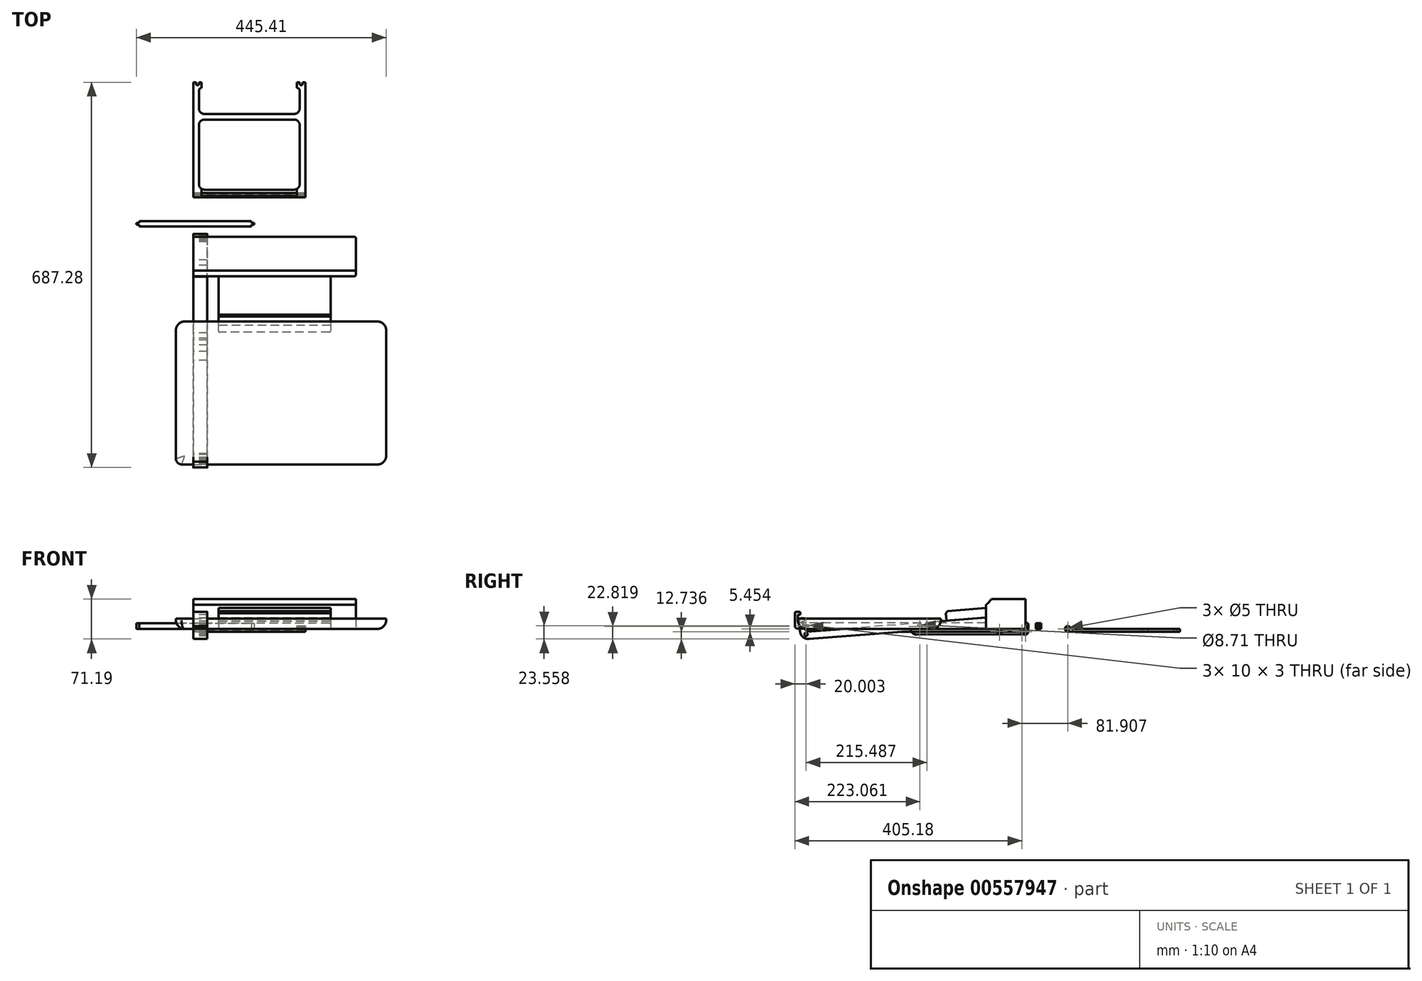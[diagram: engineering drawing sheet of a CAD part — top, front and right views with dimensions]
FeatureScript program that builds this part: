
annotation { "Feature Type Name" : "Feature", "Feature Type Description" : "" }
export const myFeature = defineFeature(function(context is Context, id is Id, definition is map)
    precondition{}
    {
        {
            var Q0;
            Q0=qCreatedBy(makeId("Top.planeOp"),FACE);
            var sketch = newSketch(context, id + "F0", { "sketchPlane" : qUnion([Q0])});
            skLineSegment(sketch, "E0", {"start": v(0, 0) * mm, "end": v(290, 0) * mm});
            skLineSegment(sketch, "E1", {"start": v(290, 0) * mm, "end": v(290, -70) * mm});
            skLineSegment(sketch, "E2", {"start": v(290, -70) * mm, "end": v(245, -70) * mm});
            skLineSegment(sketch, "E3", {"start": v(245, -70) * mm, "end": v(245, -170) * mm});
            skLineSegment(sketch, "E4", {"start": v(245, -170) * mm, "end": v(45, -170) * mm});
            skLineSegment(sketch, "E5", {"start": v(45, -170) * mm, "end": v(45, -70) * mm});
            skLineSegment(sketch, "E6", {"start": v(45, -70) * mm, "end": v(0, -70) * mm});
            skLineSegment(sketch, "E7", {"start": v(0, -70) * mm, "end": v(0, 0) * mm});
            skSolve(sketch);
        }
        {
            var Q0;
            Q0=makeQuery(id+"F0.imprint","IMPRINT",FACE,{"disambiguationData":[TD([[makeQuery(id+"F0.imprint","IMPRINT",EDGE,{"derivedFrom":sQuery(id+"F0.wireOp",EDGE,"E0")}),-1.0]])]});
            extrude(context, id + "F1", {"entities" : qUnion([Q0]), "depth" : 53 * mm, "offsetDistance" : 25.4 * mm});
        }
        {
            var Q0;
            Q0=makeQuery(id+"F1.opExtrude","SWEPT_FACE",FACE,{"disambiguationData":[OSD([sQuery(id+"F0.wireOp",EDGE,"E3")])]});
            var sketch = newSketch(context, id + "F2", { "sketchPlane" : qUnion([Q0])});
            skLineSegment(sketch, "E8", {"start": v(-170, 53) * mm, "end": v(-170, 10) * mm});
            skLineSegment(sketch, "E9", {"start": v(-170, 10) * mm, "end": v(-158, 13) * mm});
            skLineSegment(sketch, "E10", {"start": v(-158, 13) * mm, "end": v(-70, 20) * mm});
            skLineSegment(sketch, "E11", {"start": v(-70, 20) * mm, "end": v(-70, 43) * mm});
            skLineSegment(sketch, "E12", {"start": v(-70, 43) * mm, "end": v(-60, 53) * mm});
            skLineSegment(sketch, "E13", {"start": v(-60, 53) * mm, "end": v(-170, 53) * mm});
            skLineSegment(sketch, "E14", {"start": v(-70, 20) * mm, "end": v(-70.44, 37.02) * mm});
            skLineSegment(sketch, "E15", {"start": v(-70.44, 37.02) * mm, "end": v(-138.98, 31.57) * mm});
            skLineSegment(sketch, "E16", {"start": v(-138.98, 31.57) * mm, "end": v(-141.82, 27.51) * mm});
            skLineSegment(sketch, "E17", {"start": v(-141.82, 27.51) * mm, "end": v(-140.78, 14.37) * mm});
            skLineSegment(sketch, "E18", {"start": v(-140.78, 14.37) * mm, "end": v(-70, 20) * mm});
            skSolve(sketch);
        }
        {
            var Q0;
            Q0 = qSketchRegion(id + "F2", true);
            extrude(context, id + "F3", {"entities" : qUnion([Q0]), "depth" : 70 * mm, "offsetDistance" : 25 * mm, "hasSecondDirection" : true, "secondDirectionOppositeDirection" : true, "secondDirectionDepth" : 250 * mm});
        }
        {
            var Q0;
            Q0=makeQuery(id+"F3.opExtrude","SWEPT_BODY",BODY,{"disambiguationData":[OSD([sQuery(id+"F2.wireOp",EDGE,"E8"),sQuery(id+"F2.wireOp",EDGE,"E9"),sQuery(id+"F2.wireOp",EDGE,"E10"),sQuery(id+"F2.wireOp",EDGE,"E11"),sQuery(id+"F2.wireOp",EDGE,"E12"),sQuery(id+"F2.wireOp",EDGE,"E13")])]});
            var Q1;
            Q1=makeQuery(id+"F1.opExtrude","SWEPT_BODY",BODY,{"disambiguationData":[OSD([sQuery(id+"F0.wireOp",EDGE,"E0"),sQuery(id+"F0.wireOp",EDGE,"E1"),sQuery(id+"F0.wireOp",EDGE,"E2"),sQuery(id+"F0.wireOp",EDGE,"E3"),sQuery(id+"F0.wireOp",EDGE,"E4"),sQuery(id+"F0.wireOp",EDGE,"E5"),sQuery(id+"F0.wireOp",EDGE,"E6"),sQuery(id+"F0.wireOp",EDGE,"E7")])]});
            booleanBodies(context, id + "F4", {"operationType" : BooleanOperationType.SUBTRACTION, "tools" : qUnion([Q0]), "targets" : qUnion([Q1])});
        }
        {
            var Q0;
            Q0=makeQuery(id+"F1.opExtrude","SWEPT_EDGE",EDGE,{"disambiguationData":[OSD([sQuery(id+"F0.wireOp",EDGE,"E3"),sQuery(id+"F0.wireOp",EDGE,"E4")])]});
            var Q1;
            Q1=makeQuery(id+"F1.opExtrude","SWEPT_EDGE",EDGE,{"disambiguationData":[OSD([sQuery(id+"F0.wireOp",EDGE,"E1"),sQuery(id+"F0.wireOp",EDGE,"E2")])]});
            var Q2;
            Q2=makeQuery(id+"F1.opExtrude","SWEPT_EDGE",EDGE,{"disambiguationData":[OSD([sQuery(id+"F0.wireOp",EDGE,"E0"),sQuery(id+"F0.wireOp",EDGE,"E1")])]});
            var Q3;
            Q3=makeQuery(id+"F1.opExtrude","SWEPT_EDGE",EDGE,{"disambiguationData":[OSD([sQuery(id+"F0.wireOp",EDGE,"E0"),sQuery(id+"F0.wireOp",EDGE,"E7")])]});
            var Q4;
            Q4=makeQuery(id+"F1.opExtrude","SWEPT_EDGE",EDGE,{"disambiguationData":[OSD([sQuery(id+"F0.wireOp",EDGE,"E6"),sQuery(id+"F0.wireOp",EDGE,"E7")])]});
            var Q5;
            Q5=makeQuery(id+"F1.opExtrude","SWEPT_EDGE",EDGE,{"disambiguationData":[OSD([sQuery(id+"F0.wireOp",EDGE,"E4"),sQuery(id+"F0.wireOp",EDGE,"E5")])]});
            fillet(context, id + "F5", {"entities" : qUnion([Q0, Q1, Q2, Q3, Q4, Q5]), "radius" : 2 * mm, "tangentPropagation" : true, "allowEdgeOverflow" : false});
        }
        {
            var Q0;
            Q0=qCreatedBy(makeId("Right.planeOp"),FACE);
            var sketch = newSketch(context, id + "F6", { "sketchPlane" : qUnion([Q0])});
            skLineSegment(sketch, "E19", {"start": v(0.07, 10.37) * mm, "end": v(0.07, 0.37) * mm});
            skLineSegment(sketch, "E20", {"start": v(0.07, 0.37) * mm, "end": v(-70.93, 0.37) * mm});
            skLineSegment(sketch, "E21", {"start": v(-70.93, 0.37) * mm, "end": v(-70.93, 10.37) * mm});
            skLineSegment(sketch, "E22", {"start": v(-70.93, 10.37) * mm, "end": v(-396.42, 10.37) * mm});
            skLineSegment(sketch, "E23", {"start": v(-406.42, 20.37) * mm, "end": v(-406.42, 25.18) * mm});
            skLineSegment(sketch, "E24", {"start": v(-403.42, 30.18) * mm, "end": v(-409.42, 30.18) * mm});
            skLineSegment(sketch, "E25", {"start": v(-411.42, 28.18) * mm, "end": v(-411.42, 4.95) * mm});
            skLineSegment(sketch, "E26", {"start": v(-406.43, 0.37) * mm, "end": v(-206.4, 0.37) * mm});
            skLineSegment(sketch, "E27", {"start": v(5.07, 0.23) * mm, "end": v(5.07, 8.37) * mm});
            skLineSegment(sketch, "E28", {"start": v(3.07, 10.37) * mm, "end": v(0.07, 10.37) * mm});
            skPoint(sketch, "E29.visualSharp", {"position": v(-406.42, 10.37) * mm});
            skArc(sketch, "E29.filletArc", {"start": v(-406.42, 20.37) * mm, "mid": v(-403.49, 13.3) * mm, "end": v(-396.42, 10.37) * mm});
            skPoint(sketch, "E30.visualSharp", {"position": v(5.07, -9.63) * mm});
            skArc(sketch, "E30.filletArc", {"start": v(-6.24, -9.69) * mm, "mid": v(1.66, -7.3) * mm, "end": v(5.07, 0.23) * mm});
            skPoint(sketch, "E31.visualSharp", {"position": v(-411.42, 30.18) * mm});
            skArc(sketch, "E31.filletArc", {"start": v(-409.42, 30.18) * mm, "mid": v(-410.83, 29.6) * mm, "end": v(-411.42, 28.18) * mm});
            skPoint(sketch, "E32.visualSharp", {"position": v(5.07, 10.37) * mm});
            skArc(sketch, "E32.filletArc", {"start": v(5.07, 8.37) * mm, "mid": v(4.48, 9.78) * mm, "end": v(3.07, 10.37) * mm});
            skLineSegment(sketch, "E33.bottom", {"start": v(-386.42, 6.87) * mm, "end": v(-396.42, 6.87) * mm});
            skLineSegment(sketch, "E33.top", {"start": v(-386.42, 3.87) * mm, "end": v(-396.42, 3.87) * mm});
            skLineSegment(sketch, "E33.left", {"start": v(-386.42, 6.87) * mm, "end": v(-386.42, 3.87) * mm});
            skLineSegment(sketch, "E33.right", {"start": v(-396.42, 6.87) * mm, "end": v(-396.42, 3.87) * mm});
            skLineSegment(sketch, "E34.filletArc", {"start": v(-380.93, 2.65) * mm, "end": v(-380.93, 2.65) * mm});
            skLineSegment(sketch, "E35.bottom", {"start": v(-170.93, 6.87) * mm, "end": v(-180.93, 6.87) * mm});
            skLineSegment(sketch, "E35.top", {"start": v(-170.93, 3.87) * mm, "end": v(-180.93, 3.87) * mm});
            skLineSegment(sketch, "E35.left", {"start": v(-170.93, 6.87) * mm, "end": v(-170.93, 3.87) * mm});
            skLineSegment(sketch, "E35.right", {"start": v(-180.93, 6.87) * mm, "end": v(-180.93, 3.87) * mm});
            skLineSegment(sketch, "E36.bottom", {"start": v(-40.88, -3.13) * mm, "end": v(-50.88, -3.13) * mm});
            skLineSegment(sketch, "E36.top", {"start": v(-40.88, -6.13) * mm, "end": v(-50.88, -6.13) * mm});
            skLineSegment(sketch, "E36.left", {"start": v(-40.88, -3.13) * mm, "end": v(-40.88, -6.13) * mm});
            skLineSegment(sketch, "E36.right", {"start": v(-50.88, -3.13) * mm, "end": v(-50.88, -6.13) * mm});
            skCircle(sketch, "E37", {"center": v(-6.24, -4.69) * mm, "radius": 2.5 * mm});
            skLineSegment(sketch, "E38", {"start": v(-194.37, -10.19) * mm, "end": v(-6.24, -9.69) * mm});
            skLineSegment(sketch, "E39", {"start": v(-406.42, 25.18) * mm, "end": v(-403.42, 25.18) * mm});
            skLineSegment(sketch, "E40", {"start": v(-401.42, 27.18) * mm, "end": v(-401.42, 28.18) * mm});
            skPoint(sketch, "E41.visualSharp", {"position": v(-401.42, 30.18) * mm});
            skArc(sketch, "E41.filletArc", {"start": v(-401.42, 28.18) * mm, "mid": v(-402, 29.6) * mm, "end": v(-403.42, 30.18) * mm});
            skPoint(sketch, "E42.visualSharp", {"position": v(-401.42, 25.18) * mm});
            skArc(sketch, "E42.filletArc", {"start": v(-403.42, 25.18) * mm, "mid": v(-402, 25.77) * mm, "end": v(-401.42, 27.18) * mm});
            skLineSegment(sketch, "E43", {"start": v(-204.4, -0.19) * mm, "end": v(-204.4, -1.63) * mm});
            skPoint(sketch, "E44.visualSharp", {"position": v(-204.4, -10.21) * mm});
            skArc(sketch, "E44.filletArc", {"start": v(-204.4, -0.19) * mm, "mid": v(-201.46, -7.27) * mm, "end": v(-194.37, -10.19) * mm});
            skPoint(sketch, "E45.visualSharp", {"position": v(-204.4, 0.37) * mm});
            skArc(sketch, "E45.filletArc", {"start": v(-204.4, -1.63) * mm, "mid": v(-204.98, -0.22) * mm, "end": v(-206.4, 0.37) * mm});
            skArc(sketch, "E46", {"start": v(-411.42, 4.95) * mm, "mid": v(-409.82, 1.69) * mm, "end": v(-406.43, 0.37) * mm});
            skSolve(sketch);
        }
        {
            var Q0;
            Q0=makeQuery(id+"F6.imprint","IMPRINT",FACE,{"disambiguationData":[TD([[makeQuery(id+"F6.imprint","IMPRINT",EDGE,{"derivedFrom":sQuery(id+"F6.wireOp",EDGE,"E19")}),1.0]])]});
            extrude(context, id + "F7", {"entities" : qUnion([Q0]), "depth" : 25 * mm, "offsetDistance" : 25 * mm});
        }
        {
            var Q0;
            Q0=qCreatedBy(makeId("Top.planeOp"),FACE);
            var sketch = newSketch(context, id + "F8", { "sketchPlane" : qUnion([Q0])});
            skLineSegment(sketch, "E47", {"start": v(103.7, 27.93) * mm, "end": v(-96.3, 27.93) * mm});
            skLineSegment(sketch, "E48", {"start": v(-96.3, 27.93) * mm, "end": v(-96.3, 24.93) * mm});
            skLineSegment(sketch, "E49", {"start": v(-96.3, 24.93) * mm, "end": v(-101.3, 24.93) * mm});
            skLineSegment(sketch, "E50", {"start": v(-101.3, 24.93) * mm, "end": v(-101.3, 21.93) * mm});
            skLineSegment(sketch, "E51", {"start": v(-101.3, 21.93) * mm, "end": v(-96.3, 21.93) * mm});
            skLineSegment(sketch, "E52", {"start": v(-96.3, 21.93) * mm, "end": v(-96.3, 18.93) * mm});
            skLineSegment(sketch, "E53", {"start": v(-96.3, 18.93) * mm, "end": v(103.7, 18.93) * mm});
            skLineSegment(sketch, "E54", {"start": v(103.7, 18.93) * mm, "end": v(103.7, 21.93) * mm});
            skLineSegment(sketch, "E55", {"start": v(103.7, 21.93) * mm, "end": v(108.7, 21.93) * mm});
            skLineSegment(sketch, "E56", {"start": v(108.7, 21.93) * mm, "end": v(108.7, 24.93) * mm});
            skLineSegment(sketch, "E57", {"start": v(108.7, 24.93) * mm, "end": v(103.7, 24.93) * mm});
            skLineSegment(sketch, "E58", {"start": v(103.7, 24.93) * mm, "end": v(103.7, 27.93) * mm});
            skSolve(sketch);
        }
        {
            var Q0;
            Q0 = qSketchRegion(id + "F8", true);
            extrude(context, id + "F9", {"entities" : qUnion([Q0]), "depth" : 10 * mm, "offsetDistance" : 25 * mm});
        }
        {
            var Q0;
            Q0=qCreatedBy(makeId("Right.planeOp"),FACE);
            var sketch = newSketch(context, id + "F10", { "sketchPlane" : qUnion([Q0])});
            skLineSegment(sketch, "E59.bottom", {"start": v(71.73, 71.48) * mm, "end": v(83.68, 71.48) * mm});
            skLineSegment(sketch, "E59.top", {"start": v(71.73, 63) * mm, "end": v(83.68, 63) * mm});
            skLineSegment(sketch, "E59.left", {"start": v(71.73, 71.48) * mm, "end": v(71.73, 63) * mm});
            skLineSegment(sketch, "E59.right", {"start": v(83.68, 71.48) * mm, "end": v(83.68, 63) * mm});
            skLineSegment(sketch, "E60", {"start": v(-71, 19.86) * mm, "end": v(-382.03, -4.78) * mm});
            skLineSegment(sketch, "E61", {"start": v(-398.16, 8.99) * mm, "end": v(-398.56, 13.97) * mm});
            skLineSegment(sketch, "E62", {"start": v(-398.56, 13.97) * mm, "end": v(-395.57, 14.2) * mm});
            skLineSegment(sketch, "E63", {"start": v(-393.73, 16.36) * mm, "end": v(-393.81, 17.36) * mm});
            skLineSegment(sketch, "E64", {"start": v(-395.96, 19.2) * mm, "end": v(-398.95, 18.95) * mm});
            skLineSegment(sketch, "E65", {"start": v(-403.54, 13.57) * mm, "end": v(-402.12, -4.38) * mm});
            skLineSegment(sketch, "E66", {"start": v(-385.98, -18.14) * mm, "end": v(-220.07, -5) * mm});
            skLineSegment(sketch, "E67", {"start": v(-220.07, -5) * mm, "end": v(-8.9, -5) * mm});
            skLineSegment(sketch, "E68", {"start": v(5, -5.45) * mm, "end": v(5, 3) * mm});
            skLineSegment(sketch, "E69", {"start": v(3, 5) * mm, "end": v(2, 5) * mm});
            skLineSegment(sketch, "E70", {"start": v(0, 3) * mm, "end": v(0, 0) * mm});
            skLineSegment(sketch, "E71", {"start": v(0, 0) * mm, "end": v(-71, 0) * mm});
            skLineSegment(sketch, "E72", {"start": v(-71, 0) * mm, "end": v(-71, 19.86) * mm});
            skPoint(sketch, "E73.visualSharp", {"position": v(-396.98, -5.97) * mm});
            skArc(sketch, "E73.filletArc", {"start": v(-398.16, 8.99) * mm, "mid": v(-392.95, -1.24) * mm, "end": v(-382.03, -4.78) * mm});
            skPoint(sketch, "E74.visualSharp", {"position": v(-400.94, -19.33) * mm});
            skArc(sketch, "E74.filletArc", {"start": v(-402.12, -4.38) * mm, "mid": v(-396.9, -14.6) * mm, "end": v(-385.98, -18.14) * mm});
            skPoint(sketch, "E75.visualSharp", {"position": v(-403.94, 18.56) * mm});
            skArc(sketch, "E75.filletArc", {"start": v(-398.95, 18.95) * mm, "mid": v(-402.36, 17.22) * mm, "end": v(-403.54, 13.57) * mm});
            skPoint(sketch, "E76.visualSharp", {"position": v(-393.97, 19.35) * mm});
            skArc(sketch, "E76.filletArc", {"start": v(-393.81, 17.36) * mm, "mid": v(-394.5, 18.72) * mm, "end": v(-395.96, 19.2) * mm});
            skPoint(sketch, "E77.visualSharp", {"position": v(-393.57, 14.36) * mm});
            skArc(sketch, "E77.filletArc", {"start": v(-395.57, 14.2) * mm, "mid": v(-394.2, 14.9) * mm, "end": v(-393.73, 16.36) * mm});
            skPoint(sketch, "E78.visualSharp", {"position": v(5, 5) * mm});
            skArc(sketch, "E78.filletArc", {"start": v(5, 3) * mm, "mid": v(4.41, 4.41) * mm, "end": v(3, 5) * mm});
            skCircle(sketch, "E79", {"center": v(-391.52, -9.76) * mm, "radius": 2.88 * mm});
            skPoint(sketch, "E80.visualSharp", {"position": v(0, 5) * mm});
            skArc(sketch, "E80.filletArc", {"start": v(2, 5) * mm, "mid": v(0.59, 4.41) * mm, "end": v(0, 3) * mm});
            skCircle(sketch, "E81", {"center": v(-188.36, 4.63) * mm, "radius": 4.35 * mm});
            skArc(sketch, "E82", {"start": v(-4.45, -7.73) * mm, "mid": v(1.17, -10.32) * mm, "end": v(5, -5.45) * mm});
            skCircle(sketch, "E83", {"center": v(0, -5.45) * mm, "radius": 2.5 * mm});
            skPoint(sketch, "E84.visualSharp", {"position": v(-4.98, -5) * mm});
            skArc(sketch, "E84.filletArc", {"start": v(-4.45, -7.73) * mm, "mid": v(-6.3, -5.74) * mm, "end": v(-8.9, -5) * mm});
            skSolve(sketch);
        }
        {
            var Q0;
            Q0 = qSketchRegion(id + "F10", true);
            extrude(context, id + "F11", {"entities" : qUnion([Q0]), "depth" : 25 * mm, "offsetDistance" : 25 * mm});
        }
        {
            var Q0;
            Q0=makeQuery(id+"F2.imprint","IMPRINT",FACE,{"disambiguationData":[TD([[makeQuery(id+"F2.imprint","IMPRINT",EDGE,{"derivedFrom":sQuery(id+"F2.wireOp",EDGE,"E14")}),1.0]])]});
            extrude(context, id + "F12", {"entities" : qUnion([Q0]), "depth" : 0 * mm, "offsetDistance" : 25 * mm, "hasSecondDirection" : true, "secondDirectionOppositeDirection" : true, "secondDirectionDepth" : 200 * mm});
        }
        {
            var Q0;
            Q0=qCreatedBy(makeId("Top.planeOp"),FACE);
            var sketch = newSketch(context, id + "F13", { "sketchPlane" : qUnion([Q0])});
            skLineSegment(sketch, "E85.bottom", {"start": v(-15.89, -151.03) * mm, "end": v(329.11, -151.03) * mm});
            skLineSegment(sketch, "E85.top", {"start": v(-20.89, -406.03) * mm, "end": v(329.11, -406.03) * mm});
            skLineSegment(sketch, "E85.left", {"start": v(-30.89, -166.03) * mm, "end": v(-30.89, -396.03) * mm});
            skLineSegment(sketch, "E85.right", {"start": v(344.11, -166.03) * mm, "end": v(344.11, -391.03) * mm});
            skPoint(sketch, "E86.visualSharp", {"position": v(-30.89, -151.03) * mm});
            skArc(sketch, "E86.filletArc", {"start": v(-15.89, -151.03) * mm, "mid": v(-26.5, -155.43) * mm, "end": v(-30.89, -166.03) * mm});
            skPoint(sketch, "E87.visualSharp", {"position": v(344.11, -151.03) * mm});
            skArc(sketch, "E87.filletArc", {"start": v(344.11, -166.03) * mm, "mid": v(339.72, -155.43) * mm, "end": v(329.11, -151.03) * mm});
            skPoint(sketch, "E88.visualSharp", {"position": v(344.11, -406.03) * mm});
            skArc(sketch, "E88.filletArc", {"start": v(329.11, -406.03) * mm, "mid": v(339.72, -401.64) * mm, "end": v(344.11, -391.03) * mm});
            skPoint(sketch, "E89.visualSharp", {"position": v(-30.89, -406.03) * mm});
            skArc(sketch, "E89.filletArc", {"start": v(-30.89, -396.03) * mm, "mid": v(-27.96, -403.1) * mm, "end": v(-20.89, -406.03) * mm});
            skSolve(sketch);
        }
        {
            var Q0;
            Q0=makeQuery(id+"F13.imprint","IMPRINT",FACE,{"disambiguationData":[TD([[makeQuery(id+"F13.imprint","IMPRINT",EDGE,{"derivedFrom":sQuery(id+"F13.wireOp",EDGE,"E85.bottom")}),-1.0]])]});
            extrude(context, id + "F14", {"entities" : qUnion([Q0]), "depth" : 18 * mm, "offsetDistance" : 25 * mm});
        }
        {
            var Q0;
            Q0=makeQuery(id+"F14.opExtrude","CAP_EDGE",EDGE,{"disambiguationData":[OSD([sQuery(id+"F13.wireOp",EDGE,"E85.top")])],"isStart":true});
            fillet(context, id + "F15", {"entities" : qUnion([Q0]), "radius" : 15 * mm, "tangentPropagation" : true, "allowEdgeOverflow" : false});
        }
        {
            var Q0;
            Q0=makeQuery(id+"F11.opExtrude","SWEPT_BODY",BODY,{"disambiguationData":[OSD([sQuery(id+"F10.wireOp",EDGE,"E59.bottom"),sQuery(id+"F10.wireOp",EDGE,"E59.top"),sQuery(id+"F10.wireOp",EDGE,"E59.left"),sQuery(id+"F10.wireOp",EDGE,"E59.right")])]});
            deleteBodies(context, id + "F16", {"entities" : qUnion([Q0])});
        }
        {
            var Q0;
            Q0=qCreatedBy(makeId("Right.planeOp"),FACE);
            var sketch = newSketch(context, id + "F17", { "sketchPlane" : qUnion([Q0])});
            skArc(sketch, "E90", {"start": v(80, 2.5) * mm, "mid": v(71.3, 2.42) * mm, "end": v(75.86, -5) * mm});
            skLineSegment(sketch, "E91", {"start": v(75.86, -5) * mm, "end": v(275.86, -5) * mm});
            skLineSegment(sketch, "E92", {"start": v(275.86, -5) * mm, "end": v(275.86, 0) * mm});
            skLineSegment(sketch, "E93", {"start": v(275.86, 0) * mm, "end": v(84.33, 0) * mm});
            skCircle(sketch, "E94", {"center": v(75.67, 0) * mm, "radius": 2.5 * mm});
            skPoint(sketch, "E95.visualSharp", {"position": v(80.67, 0) * mm});
            skArc(sketch, "E95.filletArc", {"start": v(80, 2.5) * mm, "mid": v(81.83, 0.67) * mm, "end": v(84.33, 0) * mm});
            skSolve(sketch);
        }
        {
            var Q0;
            Q0=makeQuery(id+"F17.imprint","IMPRINT",FACE,{"disambiguationData":[TD([[makeQuery(id+"F17.imprint","IMPRINT",EDGE,{"derivedFrom":sQuery(id+"F17.wireOp",EDGE,"E90")}),1.0]])]});
            extrude(context, id + "F18", {"entities" : qUnion([Q0]), "depth" : 200 * mm, "offsetDistance" : 25 * mm});
        }
        {
            var Q0;
            Q0=makeQuery(id+"F18.opExtrude","SWEPT_FACE",FACE,{"disambiguationData":[OSD([sQuery(id+"F17.wireOp",EDGE,"E93")])]});
            var sketch = newSketch(context, id + "F19", { "sketchPlane" : qUnion([Q0])});
            skLineSegment(sketch, "E96.bottom", {"start": v(15, 265.86) * mm, "end": v(15, 265.86) * mm});
            skLineSegment(sketch, "E96.top", {"start": v(20, 219.4) * mm, "end": v(180, 219.4) * mm});
            skLineSegment(sketch, "E96.left", {"start": v(10, 260.86) * mm, "end": v(10, 229.4) * mm});
            skLineSegment(sketch, "E96.right", {"start": v(190, 260.86) * mm, "end": v(190, 229.4) * mm});
            skLineSegment(sketch, "E97.bottom", {"start": v(20, 209.4) * mm, "end": v(180, 209.4) * mm});
            skLineSegment(sketch, "E97.top", {"start": v(20, 84.33) * mm, "end": v(180, 84.33) * mm});
            skLineSegment(sketch, "E97.left", {"start": v(10, 199.4) * mm, "end": v(10, 94.33) * mm});
            skLineSegment(sketch, "E97.right", {"start": v(190, 199.4) * mm, "end": v(190, 94.33) * mm});
            skLineSegment(sketch, "E98.bottom", {"start": v(15, 275.87) * mm, "end": v(185, 275.87) * mm});
            skLineSegment(sketch, "E98.left", {"start": v(15, 275.87) * mm, "end": v(15, 265.86) * mm});
            skLineSegment(sketch, "E98.right", {"start": v(185, 275.87) * mm, "end": v(185, 265.86) * mm});
            skLineSegment(sketch, "E99.bottom", {"start": v(5, 275.86) * mm, "end": v(10, 275.86) * mm});
            skLineSegment(sketch, "E99.top", {"start": v(7, 270.86) * mm, "end": v(8, 270.86) * mm});
            skLineSegment(sketch, "E99.left", {"start": v(5, 275.86) * mm, "end": v(5, 272.86) * mm});
            skLineSegment(sketch, "E99.right", {"start": v(10, 275.86) * mm, "end": v(10, 272.86) * mm});
            skLineSegment(sketch, "E100.bottom", {"start": v(190, 275.86) * mm, "end": v(195, 275.86) * mm});
            skLineSegment(sketch, "E100.top", {"start": v(192, 270.86) * mm, "end": v(193, 270.86) * mm});
            skLineSegment(sketch, "E100.left", {"start": v(190, 275.86) * mm, "end": v(190, 272.86) * mm});
            skLineSegment(sketch, "E100.right", {"start": v(195, 275.86) * mm, "end": v(195, 272.86) * mm});
            skLineSegment(sketch, "E101.trimOffspring", {"start": v(185, 265.86) * mm, "end": v(185, 265.86) * mm});
            skPoint(sketch, "E102.visualSharp", {"position": v(10, 209.4) * mm});
            skArc(sketch, "E102.filletArc", {"start": v(20, 209.4) * mm, "mid": v(12.93, 206.47) * mm, "end": v(10, 199.4) * mm});
            skPoint(sketch, "E103.visualSharp", {"position": v(10, 84.33) * mm});
            skArc(sketch, "E103.filletArc", {"start": v(10, 94.33) * mm, "mid": v(12.93, 87.25) * mm, "end": v(20, 84.33) * mm});
            skPoint(sketch, "E104.visualSharp", {"position": v(190, 84.33) * mm});
            skArc(sketch, "E104.filletArc", {"start": v(180, 84.33) * mm, "mid": v(187.07, 87.25) * mm, "end": v(190, 94.33) * mm});
            skPoint(sketch, "E105.visualSharp", {"position": v(190, 209.4) * mm});
            skArc(sketch, "E105.filletArc", {"start": v(190, 199.4) * mm, "mid": v(187.07, 206.47) * mm, "end": v(180, 209.4) * mm});
            skPoint(sketch, "E106.visualSharp", {"position": v(190, 219.4) * mm});
            skArc(sketch, "E106.filletArc", {"start": v(180, 219.4) * mm, "mid": v(187.07, 222.33) * mm, "end": v(190, 229.4) * mm});
            skPoint(sketch, "E107.visualSharp", {"position": v(10, 219.4) * mm});
            skArc(sketch, "E107.filletArc", {"start": v(10, 229.4) * mm, "mid": v(12.93, 222.33) * mm, "end": v(20, 219.4) * mm});
            skPoint(sketch, "E108.visualSharp", {"position": v(10, 265.86) * mm});
            skArc(sketch, "E108.filletArc", {"start": v(15, 265.86) * mm, "mid": v(11.46, 264.4) * mm, "end": v(10, 260.86) * mm});
            skPoint(sketch, "E109.visualSharp", {"position": v(190, 265.86) * mm});
            skArc(sketch, "E109.filletArc", {"start": v(190, 260.86) * mm, "mid": v(188.54, 264.4) * mm, "end": v(185, 265.86) * mm});
            skPoint(sketch, "E110.visualSharp", {"position": v(190, 270.86) * mm});
            skArc(sketch, "E110.filletArc", {"start": v(190, 272.86) * mm, "mid": v(190.59, 271.45) * mm, "end": v(192, 270.86) * mm});
            skPoint(sketch, "E111.visualSharp", {"position": v(195, 270.86) * mm});
            skArc(sketch, "E111.filletArc", {"start": v(193, 270.86) * mm, "mid": v(194.41, 271.45) * mm, "end": v(195, 272.86) * mm});
            skPoint(sketch, "E112.visualSharp", {"position": v(5, 270.86) * mm});
            skArc(sketch, "E112.filletArc", {"start": v(5, 272.86) * mm, "mid": v(5.59, 271.44) * mm, "end": v(7, 270.86) * mm});
            skPoint(sketch, "E113.visualSharp", {"position": v(10, 270.86) * mm});
            skArc(sketch, "E113.filletArc", {"start": v(8, 270.86) * mm, "mid": v(9.41, 271.44) * mm, "end": v(10, 272.86) * mm});
            skSolve(sketch);
        }
        {
            var Q0;
            Q0=makeQuery(id+"F19.imprint","IMPRINT",FACE,{"disambiguationData":[TD([[makeQuery(id+"F19.imprint","IMPRINT",EDGE,{"derivedFrom":sQuery(id+"F19.wireOp",EDGE,"E97.bottom")}),-1.0]])]});
            var Q1;
            Q1=makeQuery(id+"F19.imprint","IMPRINT",FACE,{"disambiguationData":[TD([[makeQuery(id+"F19.imprint","IMPRINT",EDGE,{"derivedFrom":sQuery(id+"F19.wireOp",EDGE,"E99.bottom")}),-1.0]])]});
            var Q2;
            {var subQ0=sQuery(id+"F19.wireOp",EDGE,"E98.bottom");Q2=makeQuery(id+"F19.imprint","IMPRINT",FACE,{"disambiguationData":[TD([[makeQuery(id+"F19.imprint","IMPRINT",EDGE,{"derivedFrom":subQ0}),-1.0]])]});}
            var Q3;
            {var subQ0=sQuery(id+"F19.wireOp",EDGE,"E100.bottom");Q3=makeQuery(id+"F19.imprint","IMPRINT",FACE,{"disambiguationData":[TD([[makeQuery(id+"F19.imprint","IMPRINT",EDGE,{"derivedFrom":subQ0}),-1.0]])]});}
            var Q4;
            Q4=makeQuery(id+"F19.imprint","IMPRINT",FACE,{"disambiguationData":[TD([[makeQuery(id+"F19.imprint","IMPRINT",EDGE,{"derivedFrom":sQuery(id+"F19.wireOp",EDGE,"E100.top")}),1.0]])]});
            var Q5;
            Q5=makeQuery(id+"F19.imprint","IMPRINT",FACE,{"disambiguationData":[TD([[makeQuery(id+"F19.imprint","IMPRINT",EDGE,{"derivedFrom":sQuery(id+"F19.wireOp",EDGE,"E96.top")}),1.0]])]});
            extrude(context, id + "F20", {"entities" : qUnion([Q0, Q1, Q2, Q3, Q4, Q5]), "operationType" : NewBodyOperationType.REMOVE, "oppositeDirection" : true, "depth" : 25 * mm, "offsetDistance" : 25 * mm});
        }
        {
            var Q0;
            {var subQ1=sQuery(id+"F17.wireOp",EDGE,"E92");Q0=makeQuery(id+"F20.boolean.opBoolean","SPLIT",FACE,{"disambiguationData":[TD([makeQuery(id+"F20.opExtrude","SWEPT_FACE",FACE,{"disambiguationData":[OSD([sQuery(id+"F19.wireOp",EDGE,"E100.right")])]})])],"derivedFrom":makeQuery(id+"F18.opExtrude","SWEPT_FACE",FACE,{"disambiguationData":[OSD([subQ1])]})});}
            var sketch = newSketch(context, id + "F21", { "sketchPlane" : qUnion([Q0])});
            skLineSegment(sketch, "E114.bottom", {"start": v(-185, 5) * mm, "end": v(-15, 5) * mm});
            skLineSegment(sketch, "E114.top", {"start": v(-185, 0) * mm, "end": v(-15, 0) * mm});
            skLineSegment(sketch, "E114.left", {"start": v(-185, 5) * mm, "end": v(-185, 0) * mm});
            skLineSegment(sketch, "E114.right", {"start": v(-15, 5) * mm, "end": v(-15, 0) * mm});
            skSolve(sketch);
        }
        {
            var Q0;
            Q0=makeQuery(id+"F21.imprint","IMPRINT",FACE,{"disambiguationData":[TD([[makeQuery(id+"F21.imprint","IMPRINT",EDGE,{"derivedFrom":sQuery(id+"F21.wireOp",EDGE,"E114.bottom")}),-1.0]])]});
            extrude(context, id + "F22", {"entities" : qUnion([Q0]), "operationType" : NewBodyOperationType.REMOVE, "oppositeDirection" : true, "depth" : 230.8 * mm, "offsetDistance" : 25 * mm});
        }
    });
